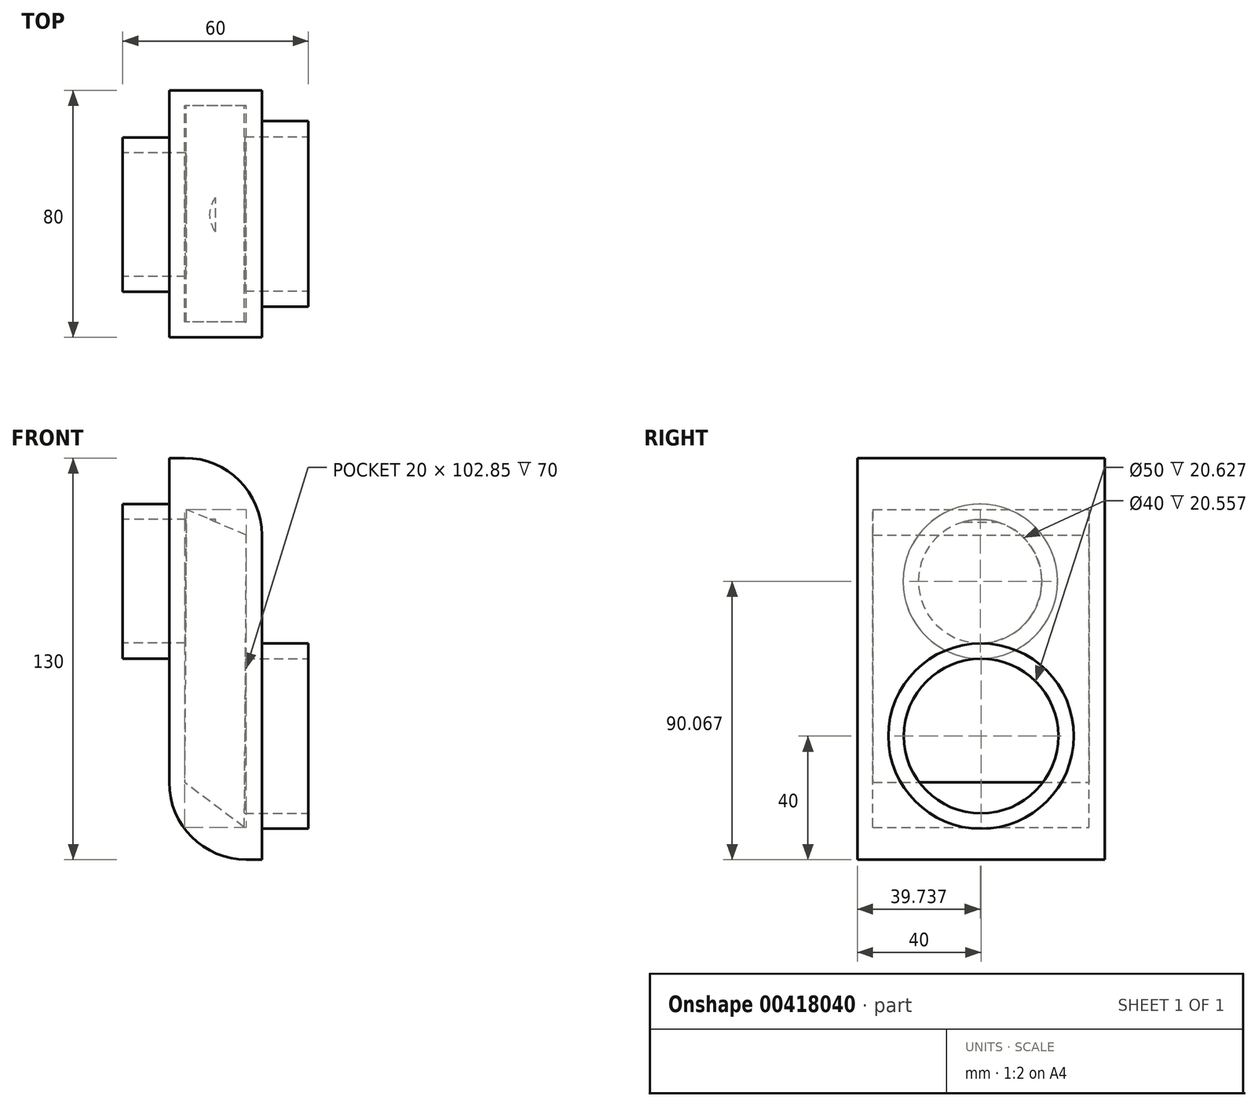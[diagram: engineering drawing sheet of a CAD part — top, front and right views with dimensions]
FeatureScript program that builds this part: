
annotation { "Feature Type Name" : "Feature", "Feature Type Description" : "" }
export const myFeature = defineFeature(function(context is Context, id is Id, definition is map)
    precondition{}
    {
        {
            assignVariable(context, id + "F0", {"name" : "boxthick", "anyValue" : 5});
        }
        {
            assignVariable(context, id + "F1", {"name" : "boxl", "anyValue" : 80});
        }
        {
            var Q0;
            Q0=qCreatedBy(makeId("Front.planeOp"),FACE);
            var sketch = newSketch(context, id + "F2", { "sketchPlane" : qUnion([Q0])});
            skLineSegment(sketch, "E0", {"start": v(0, 0) * mm, "end": v(15, 0) * mm});
            skLineSegment(sketch, "E1", {"start": v(15, 0) * mm, "end": v(15, 105) * mm});
            skLineSegment(sketch, "E2", {"start": v(0, 130) * mm, "end": v(-10, 130) * mm});
            skLineSegment(sketch, "E3", {"start": v(0, 125) * mm, "end": v(0, 125) * mm});
            skLineSegment(sketch, "E4.MirrorCS", {"start": v(-15, 130) * mm, "end": v(0, 130) * mm});
            skLineSegment(sketch, "E5.MirrorCS", {"start": v(-15, 25) * mm, "end": v(-15, 130) * mm});
            skLineSegment(sketch, "E6.MirrorCS", {"start": v(0, 5) * mm, "end": v(0, 5) * mm});
            skLineSegment(sketch, "E7.MirrorCS", {"start": v(10, 0) * mm, "end": v(0, 0) * mm});
            skPoint(sketch, "E8.visualSharp", {"position": v(15, 130) * mm});
            skArc(sketch, "E8.filletArc", {"start": v(15, 105) * mm, "mid": v(7.68, 122.68) * mm, "end": v(-10, 130) * mm});
            skPoint(sketch, "E9.visualSharp", {"position": v(10, 125) * mm});
            skPoint(sketch, "E10.visualSharp", {"position": v(-15, 0) * mm});
            skArc(sketch, "E10.filletArc", {"start": v(-15, 25) * mm, "mid": v(-7.68, 7.32) * mm, "end": v(10, 0) * mm});
            skPoint(sketch, "E11.visualSharp", {"position": v(-10, 5) * mm});
            skSolve(sketch);
        }
        {
            var Q0;
            Q0=qCreatedBy(makeId("Right.planeOp"),FACE);
            var sketch = newSketch(context, id + "F3", { "sketchPlane" : qUnion([Q0])});
            skLineSegment(sketch, "E12", {"start": v(0, 0) * mm, "end": v(-40, 0) * mm, "construction": true});
            skLineSegment(sketch, "E13", {"start": v(-40, 0) * mm, "end": v(-40, 40) * mm, "construction": true});
            skCircle(sketch, "E14", {"center": v(-40, 40) * mm, "radius": 30 * mm});
            skLineSegment(sketch, "E15", {"start": v(-40, 40) * mm, "end": v(-40, 90) * mm, "construction": true});
            skCircle(sketch, "E16", {"center": v(-40.26, 90.07) * mm, "radius": 25 * mm});
            skSolve(sketch);
        }
        {
            var Q0;
            Q0 = qSketchRegion(id + "F2", true);
            extrude(context, id + "F4", {"entities" : qUnion([Q0]), "depth" : (getVariable(context, 'boxl')) * mm, "offsetDistance" : 25 * mm});
        }
        {
            var Q0;
            Q0=qCreatedBy(makeId("Front.planeOp"),FACE);
            cPlane(context, id + "F5", {"entities" : qUnion([Q0]), "cplaneType" : CPlaneType.OFFSET, "offset" : (getVariable(context, 'boxthick')) * mm, "width" : 150 * mm, "height" : 150 * mm});
        }
        {
            var Q0;
            Q0=qCreatedBy(id+"F5.planeOp",FACE);
            var sketch = newSketch(context, id + "F6", { "sketchPlane" : qUnion([Q0])});
            skLineSegment(sketch, "E17", {"start": v(10, 105) * mm, "end": v(-9.42, 113.33) * mm});
            skLineSegment(sketch, "E18", {"start": v(-9.42, 113.33) * mm, "end": v(-10, 25) * mm});
            skLineSegment(sketch, "E19", {"start": v(9.34, 10.48) * mm, "end": v(-10, 25) * mm});
            skLineSegment(sketch, "E20", {"start": v(9.34, 10.48) * mm, "end": v(10, 105) * mm});
            skSolve(sketch);
        }
        {
            var Q0;
            Q0=makeQuery(id+"F3.imprint","IMPRINT",FACE,{"disambiguationData":[TD([[makeQuery(id+"F3.imprint","IMPRINT",EDGE,{"derivedFrom":sQuery(id+"F3.wireOp",EDGE,"E14")}),1.0]])]});
            extrude(context, id + "F7", {"entities" : qUnion([Q0]), "operationType" : NewBodyOperationType.ADD, "depth" : 30 * mm, "offsetDistance" : 25 * mm});
        }
        {
            var Q0;
            Q0=makeQuery(id+"F3.imprint","IMPRINT",FACE,{"disambiguationData":[TD([[makeQuery(id+"F3.imprint","IMPRINT",EDGE,{"derivedFrom":sQuery(id+"F3.wireOp",EDGE,"E16")}),1.0]])]});
            extrude(context, id + "F8", {"entities" : qUnion([Q0]), "operationType" : NewBodyOperationType.ADD, "oppositeDirection" : true, "depth" : 30 * mm, "offsetDistance" : 25 * mm});
        }
        {
            var Q0;
            Q0 = qSketchRegion(id + "F6", true);
            extrude(context, id + "F9", {"entities" : qUnion([Q0]), "operationType" : NewBodyOperationType.REMOVE, "depth" : (getVariable(context, 'boxl') - 2 * getVariable(context, 'boxthick')) * mm, "offsetDistance" : 25 * mm});
        }
        {
            var Q0;
            Q0=makeQuery(id+"F7.opExtrude","CAP_FACE",FACE,{"disambiguationData":[OSD([sQuery(id+"F3.wireOp",EDGE,"E14")])],"isStart":false});
            var sketch = newSketch(context, id + "F10", { "sketchPlane" : qUnion([Q0])});
            skCircle(sketch, "E21", {"center": v(-40, 40) * mm, "radius": 25 * mm});
            skSolve(sketch);
        }
        {
            var Q0;
            Q0=makeQuery(id+"F10.imprint","IMPRINT",FACE,{"disambiguationData":[TD([[makeQuery(id+"F10.imprint","IMPRINT",EDGE,{"derivedFrom":sQuery(id+"F10.wireOp",EDGE,"E21")}),1.0]])]});
            extrude(context, id + "F11", {"entities" : qUnion([Q0]), "operationType" : NewBodyOperationType.REMOVE, "oppositeDirection" : true, "depth" : 25 * mm, "offsetDistance" : 25 * mm});
        }
        {
            var Q0;
            Q0=makeQuery(id+"F8.opExtrude","CAP_FACE",FACE,{"disambiguationData":[OSD([sQuery(id+"F3.wireOp",EDGE,"E16")])],"isStart":false});
            var sketch = newSketch(context, id + "F12", { "sketchPlane" : qUnion([Q0])});
            skCircle(sketch, "E22", {"center": v(40.26, 90.07) * mm, "radius": 20 * mm});
            skSolve(sketch);
        }
        {
            var Q0;
            Q0=makeQuery(id+"F12.imprint","IMPRINT",FACE,{"disambiguationData":[TD([[makeQuery(id+"F12.imprint","IMPRINT",EDGE,{"derivedFrom":sQuery(id+"F12.wireOp",EDGE,"E22")}),1.0]])]});
            extrude(context, id + "F13", {"entities" : qUnion([Q0]), "operationType" : NewBodyOperationType.REMOVE, "oppositeDirection" : true, "depth" : 30 * mm, "offsetDistance" : 25 * mm});
        }
    });
